# Revit family: 3-740-xx - 37-740-xx - Maia (Outdoor)
name_source: partatom
category: Lighting Fixtures
revit_build: Autodesk Revit 2018 (Build: 20180423_1000(x64)
units: mm (PartAtom-declared; Revit-internal decimal feet)

## family parameters
Cut with Voids When Loaded = No
Host = Face
Light Source = No
Part Type = Normal
Room Calculation Point = No
Round Connector Dimension = Use Diameter
Shared = No

## types (4) — shared parameters
Diffuser = White Opal Glass
Lamp = LED Array
Manufacturer = Oxygen Lighting
Model = 3-740-xx-BPxx / 37-740-xx-BPxx - Maia
Other = <By Category>
URL = www.oxygenlighting.com
Wattage Comments = 13.00 W at 120 V
zero-valued in all types: Default Elevation

## per-type parameters (varying)
| type | Fixture | Metal Finish |
| 3-740-16 / 37-740-16 - Maia | 3-740 Maia IES | 16 - Gray |
| 3-740-16-BP16 / 37-740-16-BP16 - Maia | 3-740 BP Maia IES | 16 - Gray |
| 3-740-22-BP22 / 37-740-22-BP22 - Maia | 3-740 BP Maia IES | 22- Oiled Bronze |
| 3-740-22 / 37-740-22 - Maia | 3-740 Maia IES | 22- Oiled Bronze |

## geometry (parser evidence)
native form markers: Extrusion x2, Sweep x16
no freeform markers — native parametric forms only
